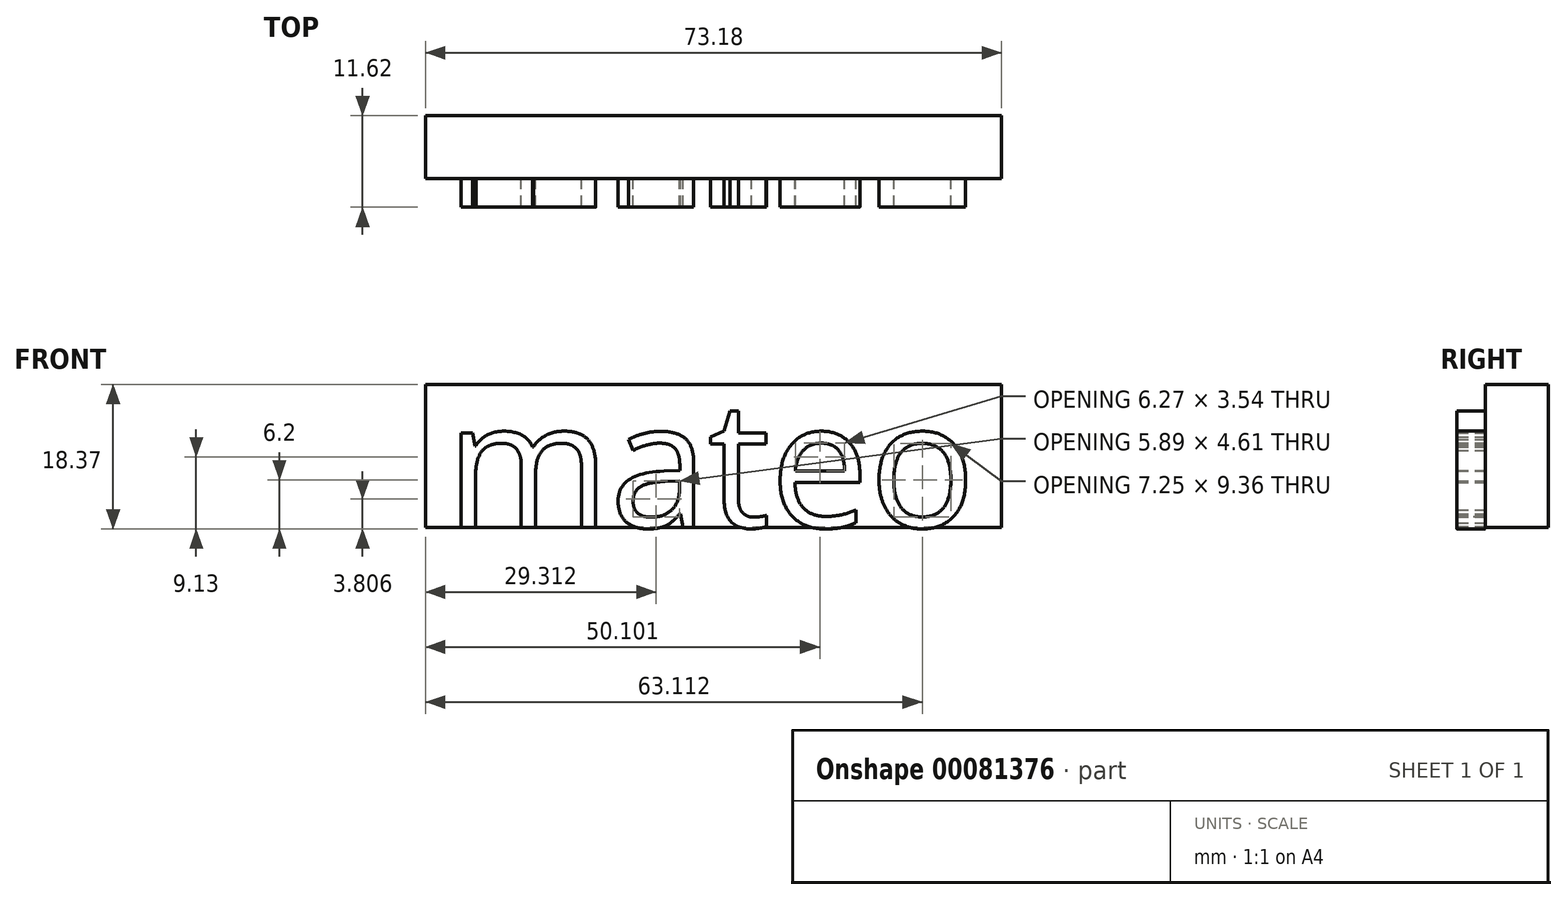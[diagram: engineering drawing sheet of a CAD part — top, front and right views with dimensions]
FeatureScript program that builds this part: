
annotation { "Feature Type Name" : "Feature", "Feature Type Description" : "" }
export const myFeature = defineFeature(function(context is Context, id is Id, definition is map)
    precondition{}
    {
        {
            var Q0;
            Q0=qCreatedBy(makeId("Front.planeOp"),FACE);
            var sketch = newSketch(context, id + "F0", { "sketchPlane" : qUnion([Q0])});
            skText(sketch, "E0", { "text": "mateo", "fontName": "OpenSans-Regular.ttf"});
            const initialGuessF0  = {"E0": [-0.0273, 0, 1, 0, 0.01612]};
            skSetInitialGuess(sketch, initialGuessF0);
            skSolve(sketch);
        }
        {
            var Q0;
            Q0 = qSketchRegion(id + "F0", true);
            extrude(context, id + "F1", {"entities" : qUnion([Q0]), "depth" : 3.62 * mm});
        }
        {
            var Q0;
            Q0=qCreatedBy(makeId("Front.planeOp"),FACE);
            var sketch = newSketch(context, id + "F2", { "sketchPlane" : qUnion([Q0])});
            skLineSegment(sketch, "E1.bottom", {"start": v(43.27, 0) * mm, "end": v(-29.91, 0) * mm});
            skLineSegment(sketch, "E1.top", {"start": v(43.27, 18.15) * mm, "end": v(-29.91, 18.15) * mm});
            skLineSegment(sketch, "E1.left", {"start": v(43.27, 0) * mm, "end": v(43.27, 18.15) * mm});
            skLineSegment(sketch, "E1.right", {"start": v(-29.91, 0) * mm, "end": v(-29.91, 18.15) * mm});
            skSolve(sketch);
        }
        {
            var Q0;
            Q0=makeQuery(id+"F2.imprint","IMPRINT",FACE,{"disambiguationData":[TD([[makeQuery(id+"F2.imprint","IMPRINT",EDGE,{"derivedFrom":sQuery(id+"F2.wireOp",EDGE,"E1.bottom")}),-1.0]])]});
            extrude(context, id + "F3", {"entities" : qUnion([Q0]), "oppositeDirection" : true, "depth" : 8 * mm});
        }
    });
